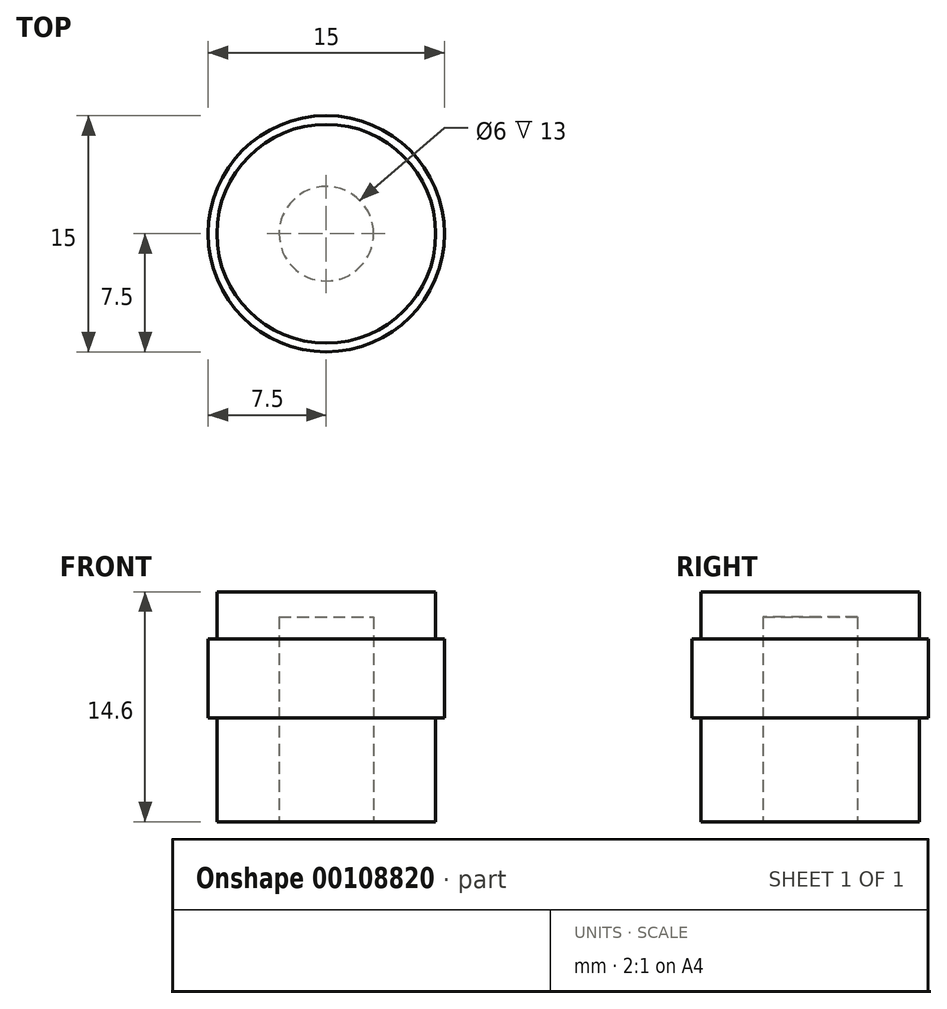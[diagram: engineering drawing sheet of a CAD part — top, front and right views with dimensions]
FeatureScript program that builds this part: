
annotation { "Feature Type Name" : "Feature", "Feature Type Description" : "" }
export const myFeature = defineFeature(function(context is Context, id is Id, definition is map)
    precondition{}
    {
        {
            var Q0;
            Q0=qCreatedBy(makeId("Top.planeOp"),FACE);
            var sketch = newSketch(context, id + "F0", { "sketchPlane" : qUnion([Q0])});
            skCircle(sketch, "E0", {"center": v(0, 0) * mm, "radius": 6.95 * mm});
            skSolve(sketch);
        }
        {
            var Q0;
            Q0 = qSketchRegion(id + "F0", true);
            extrude(context, id + "F1", {"entities" : qUnion([Q0]), "depth" : 6.6 * mm, "offsetDistance" : 25 * mm});
        }
        {
            var Q0;
            Q0=makeQuery(id+"F1.opExtrude","CAP_FACE",FACE,{"disambiguationData":[OSD([sQuery(id+"F0.wireOp",EDGE,"E0")])],"isStart":false});
            var sketch = newSketch(context, id + "F2", { "sketchPlane" : qUnion([Q0])});
            skCircle(sketch, "E1", {"center": v(0, 0) * mm, "radius": 7.5 * mm});
            skSolve(sketch);
        }
        {
            var Q0;
            Q0 = qSketchRegion(id + "F2", true);
            extrude(context, id + "F3", {"entities" : qUnion([Q0]), "operationType" : NewBodyOperationType.ADD, "depth" : 5 * mm, "offsetDistance" : 25 * mm});
        }
        {
            var Q0;
            Q0=makeQuery(id+"F3.opExtrude","CAP_FACE",FACE,{"disambiguationData":[OSD([sQuery(id+"F2.wireOp",EDGE,"E1")])],"isStart":false});
            var sketch = newSketch(context, id + "F4", { "sketchPlane" : qUnion([Q0])});
            skCircle(sketch, "E2", {"center": v(0, 0) * mm, "radius": 6.95 * mm});
            skSolve(sketch);
        }
        {
            var Q0;
            Q0 = qSketchRegion(id + "F4", true);
            extrude(context, id + "F5", {"entities" : qUnion([Q0]), "operationType" : NewBodyOperationType.ADD, "depth" : 3 * mm, "offsetDistance" : 25 * mm});
        }
        {
            var Q0;
            Q0=makeQuery(id+"F1.opExtrude","CAP_FACE",FACE,{"disambiguationData":[OSD([sQuery(id+"F0.wireOp",EDGE,"E0")])],"isStart":true});
            var sketch = newSketch(context, id + "F6", { "sketchPlane" : qUnion([Q0])});
            skCircle(sketch, "E3", {"center": v(0, 0) * mm, "radius": 3 * mm});
            skSolve(sketch);
        }
        {
            var Q0;
            Q0 = qSketchRegion(id + "F6", true);
            extrude(context, id + "F7", {"entities" : qUnion([Q0]), "operationType" : NewBodyOperationType.REMOVE, "oppositeDirection" : true, "depth" : 13 * mm, "offsetDistance" : 25 * mm});
        }
    });
